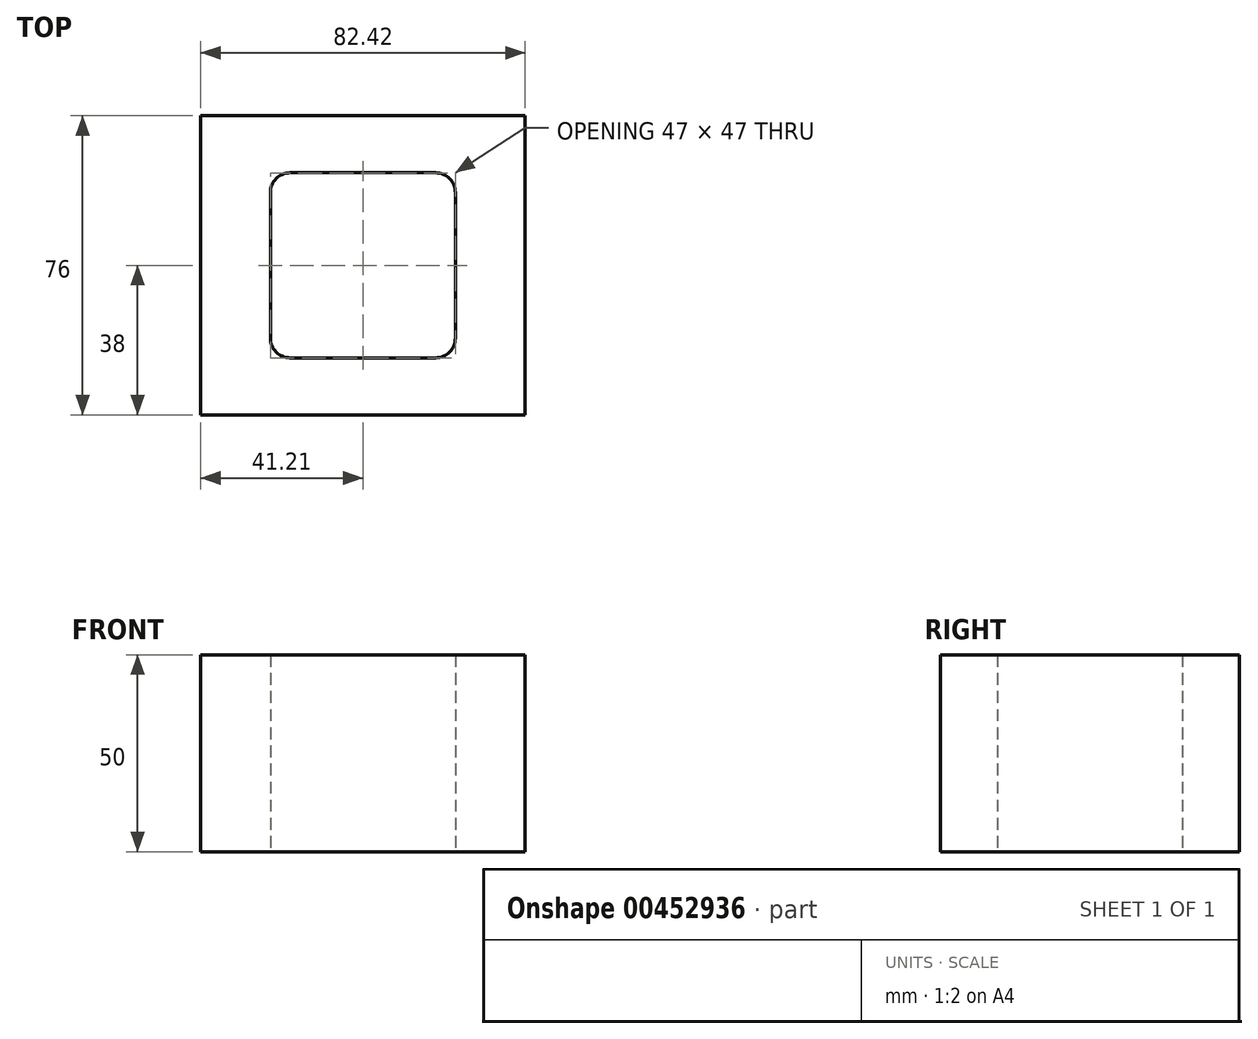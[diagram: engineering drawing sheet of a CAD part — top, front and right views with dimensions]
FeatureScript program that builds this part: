
annotation { "Feature Type Name" : "Feature", "Feature Type Description" : "" }
export const myFeature = defineFeature(function(context is Context, id is Id, definition is map)
    precondition{}
    {
        {
            var Q0;
            Q0=qCreatedBy(makeId("Top.planeOp"),FACE);
            var sketch = newSketch(context, id + "F0", { "sketchPlane" : qUnion([Q0])});
            skLineSegment(sketch, "E0.bottom", {"start": v(18.5, -23.5) * mm, "end": v(-18.5, -23.5) * mm});
            skLineSegment(sketch, "E0.top", {"start": v(18.5, 23.5) * mm, "end": v(-18.5, 23.5) * mm});
            skLineSegment(sketch, "E0.left", {"start": v(23.5, -18.5) * mm, "end": v(23.5, 18.5) * mm});
            skLineSegment(sketch, "E0.right", {"start": v(-23.5, -18.5) * mm, "end": v(-23.5, 18.5) * mm});
            skPoint(sketch, "E0.middle", {"position": v(0, 0) * mm});
            skPoint(sketch, "E1.visualSharp", {"position": v(-23.5, 23.5) * mm});
            skArc(sketch, "E1.filletArc", {"start": v(-18.5, 23.5) * mm, "mid": v(-22.04, 22.04) * mm, "end": v(-23.5, 18.5) * mm});
            skPoint(sketch, "E2.visualSharp", {"position": v(23.5, 23.5) * mm});
            skArc(sketch, "E2.filletArc", {"start": v(23.5, 18.5) * mm, "mid": v(22.04, 22.04) * mm, "end": v(18.5, 23.5) * mm});
            skPoint(sketch, "E3.visualSharp", {"position": v(23.5, -23.5) * mm});
            skArc(sketch, "E3.filletArc", {"start": v(18.5, -23.5) * mm, "mid": v(22.04, -22.04) * mm, "end": v(23.5, -18.5) * mm});
            skPoint(sketch, "E4.visualSharp", {"position": v(-23.5, -23.5) * mm});
            skArc(sketch, "E4.filletArc", {"start": v(-23.5, -18.5) * mm, "mid": v(-22.04, -22.04) * mm, "end": v(-18.5, -23.5) * mm});
            skLineSegment(sketch, "E5.bottom", {"start": v(41.2, -38) * mm, "end": v(-41.2, -38) * mm});
            skLineSegment(sketch, "E5.top", {"start": v(41.2, 38) * mm, "end": v(-41.2, 38) * mm});
            skLineSegment(sketch, "E5.left", {"start": v(41.2, -38) * mm, "end": v(41.2, 38) * mm});
            skLineSegment(sketch, "E5.right", {"start": v(-41.2, -38) * mm, "end": v(-41.2, 38) * mm});
            skSolve(sketch);
        }
        {
            var Q0;
            Q0 = qSketchRegion(id + "F0", true);
            extrude(context, id + "F1", {"entities" : qUnion([Q0]), "depth" : 50 * mm});
        }
    });
